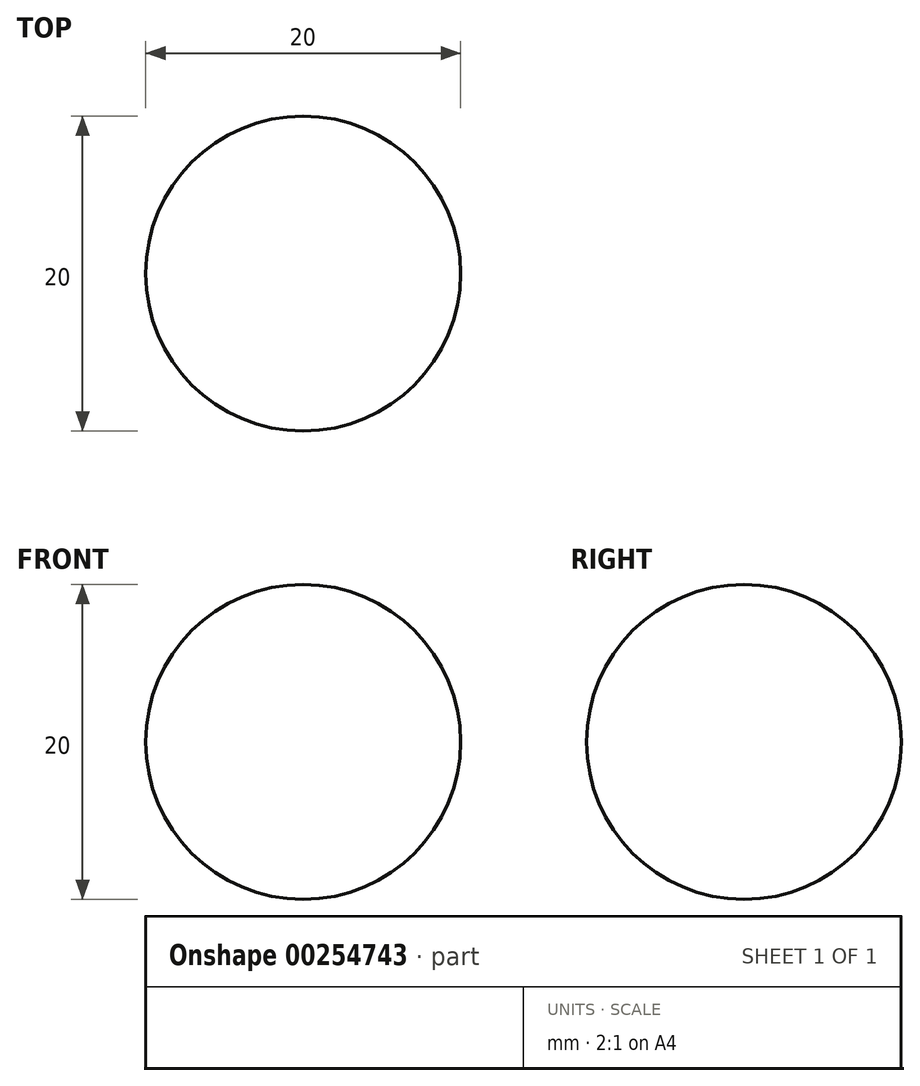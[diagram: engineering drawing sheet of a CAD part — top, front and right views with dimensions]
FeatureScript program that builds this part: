
annotation { "Feature Type Name" : "Feature", "Feature Type Description" : "" }
export const myFeature = defineFeature(function(context is Context, id is Id, definition is map)
    precondition{}
    {
        {
            var Q0;
            Q0=qCreatedBy(makeId("Front.planeOp"),FACE);
            var sketch = newSketch(context, id + "F0", { "sketchPlane" : qUnion([Q0])});
            skLineSegment(sketch, "E0", {"start": v(0, 0) * mm, "end": v(0, 20) * mm});
            skArc(sketch, "E1", {"start": v(0, 20) * mm, "mid": v(-10, 10) * mm, "end": v(0, 0) * mm});
            skSolve(sketch);
        }
        {
            var Q0;
            Q0=makeQuery(id+"F0.imprint","IMPRINT",FACE,{"disambiguationData":[TD([[makeQuery(id+"F0.imprint","IMPRINT",EDGE,{"derivedFrom":sQuery(id+"F0.wireOp",EDGE,"E0")}),1.0]])]});
            var Q1;
            Q1=sQuery(id+"F0.wireOp",EDGE,"E0");
            revolve(context, id + "F1", {"entities" : qUnion([Q0]), "axis" : qUnion([Q1]), "revolveType" : RevolveType.FULL});
        }
    });
